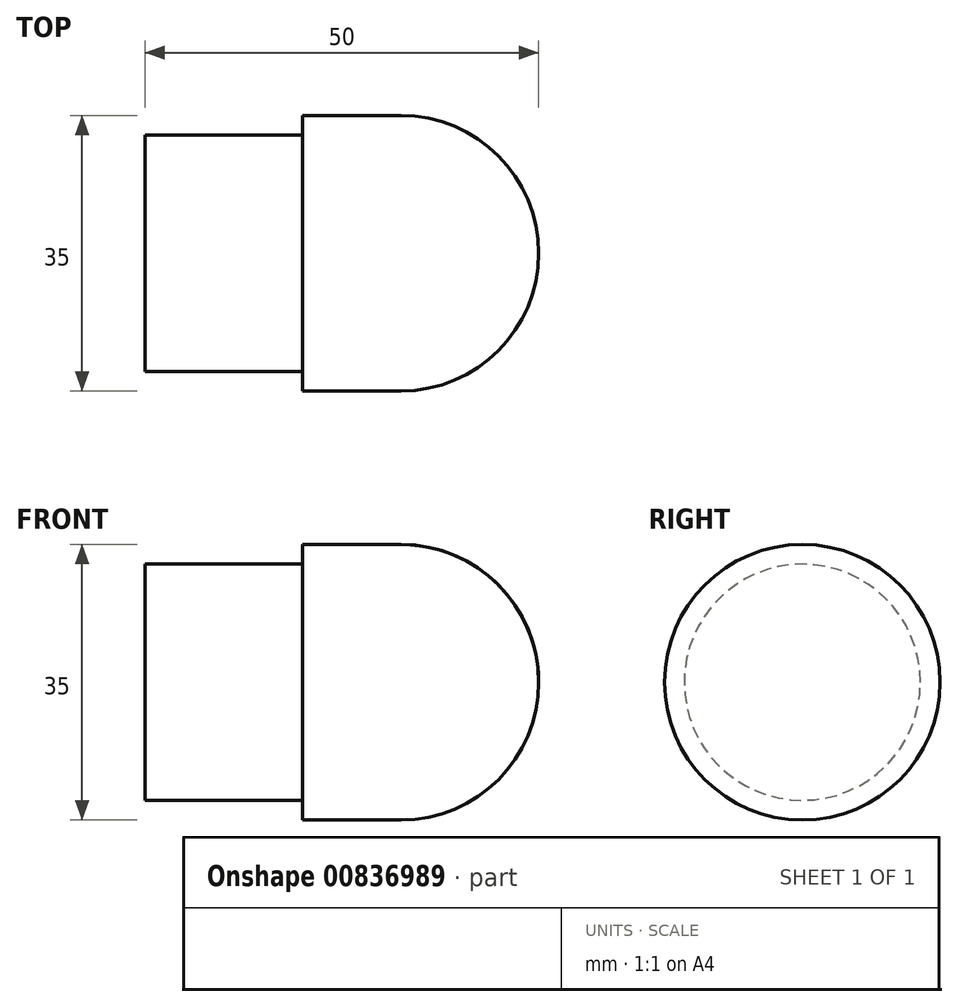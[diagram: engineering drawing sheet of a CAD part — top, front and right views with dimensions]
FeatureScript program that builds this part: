
annotation { "Feature Type Name" : "Feature", "Feature Type Description" : "" }
export const myFeature = defineFeature(function(context is Context, id is Id, definition is map)
    precondition{}
    {
        {
            var Q0;
            Q0=qCreatedBy(makeId("Front.planeOp"),FACE);
            var sketch = newSketch(context, id + "F0", { "sketchPlane" : qUnion([Q0])});
            skLineSegment(sketch, "E0.bottom", {"start": v(0, 0) * mm, "end": v(20, 0) * mm});
            skLineSegment(sketch, "E0.top", {"start": v(0, 15) * mm, "end": v(20, 15) * mm});
            skLineSegment(sketch, "E0.left", {"start": v(0, 0) * mm, "end": v(0, 15) * mm});
            skLineSegment(sketch, "E0.right", {"start": v(20, 0) * mm, "end": v(20, 15) * mm});
            skLineSegment(sketch, "E1.bottom", {"start": v(20, 0) * mm, "end": v(32.5, 0) * mm});
            skLineSegment(sketch, "E1.top", {"start": v(20, 17.5) * mm, "end": v(32.5, 17.5) * mm});
            skLineSegment(sketch, "E1.left", {"start": v(20, 0) * mm, "end": v(20, 17.5) * mm});
            skLineSegment(sketch, "E1.right", {"start": v(32.5, 0) * mm, "end": v(32.5, 17.5) * mm});
            skArc(sketch, "E2", {"start": v(50, 0) * mm, "mid": v(44.87, 12.37) * mm, "end": v(32.5, 17.5) * mm});
            skLineSegment(sketch, "E3", {"start": v(32.5, 0) * mm, "end": v(50, 0) * mm});
            skSolve(sketch);
        }
        {
            var Q0;
            Q0 = qSketchRegion(id + "F0", true);
            var Q1;
            Q1=sQuery(id+"F0.wireOp",EDGE,"E3");
            revolve(context, id + "F1", {"surfaceOperationType" : NewSurfaceOperationType.NEW, "entities" : qUnion([Q0]), "axis" : qUnion([Q1]), "revolveType" : RevolveType.FULL});
        }
    });
